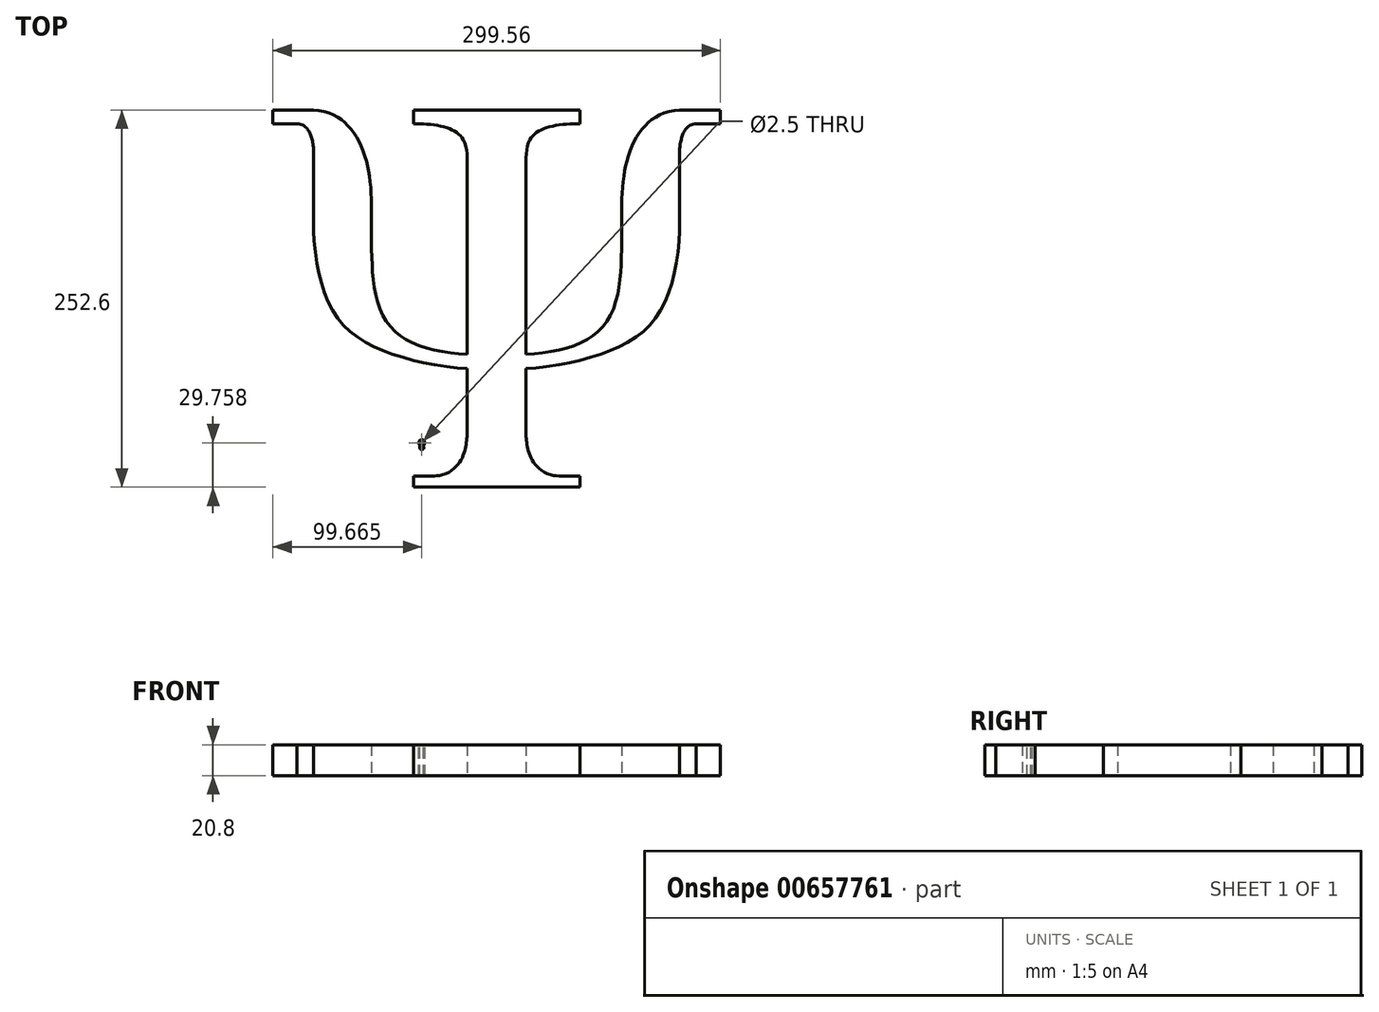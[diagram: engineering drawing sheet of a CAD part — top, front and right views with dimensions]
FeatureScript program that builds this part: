
annotation { "Feature Type Name" : "Feature", "Feature Type Description" : "" }
export const myFeature = defineFeature(function(context is Context, id is Id, definition is map)
    precondition{}
    {
        {
            var Q0;
            Q0=qCreatedBy(makeId("Top.planeOp"),FACE);
            var sketch = newSketch(context, id + "F0", { "sketchPlane" : qUnion([Q0])});
            skLineSegment(sketch, "E0", {"start": v(31.77, -358.04) * mm, "end": v(165.62, -358.04) * mm});
            skLineSegment(sketch, "E1", {"start": v(165.62, -358.04) * mm, "end": v(165.62, -340.15) * mm});
            skLineSegment(sketch, "E2", {"start": v(165.62, -340.15) * mm, "end": v(136.3, -340.15) * mm});
            skLineSegment(sketch, "E3", {"start": v(79.25, 172.15) * mm, "end": v(79.25, -144.4) * mm});
            skFitSpline(sketch, "E4", {"points": [v(136.3, -340.15) * mm, v(128.38, -339.91) * mm, v(119.4, -338.15) * mm, v(107.57, -333.31) * mm, v(99.35, -327.3) * mm, v(93.45, -321.03) * mm, v(88.64, -313.83) * mm, v(85.88, -307.88) * mm, v(83.44, -301.15) * mm, v(82.12, -296.14) * mm, v(81.06, -290.81) * mm, v(80.33, -285.89) * mm, v(79.76, -281.1) * mm, v(79.25, -276.66) * mm], "startDerivative": vector(-97.78, -0.06) * mm, "endDerivative": vector(-8.44, 72.43) * mm});
            skLineSegment(sketch, "E5", {"start": v(165.7, 249.18) * mm, "end": v(165.7, 226.82) * mm});
            skFitSpline(sketch, "E6", {"points": [v(79.25, 172.15) * mm, v(79.89, 182.32) * mm, v(81.67, 191.96) * mm, v(84.08, 198.42) * mm, v(86.92, 203.63) * mm, v(89.38, 206.86) * mm, v(92.37, 209.75) * mm, v(95.31, 212.3) * mm, v(98.88, 214.76) * mm, v(103.12, 216.98) * mm, v(108.23, 219.15) * mm, v(113.63, 221.08) * mm, v(120.47, 222.86) * mm, v(127.56, 224.26) * mm, v(134.93, 225.46) * mm, v(142.7, 226.19) * mm, v(151.51, 226.62) * mm, v(158.7, 226.91) * mm, v(165.7, 226.82) * mm], "startDerivative": vector(5.49, 144.56) * mm, "endDerivative": vector(121.24, -3.12) * mm});
            skLineSegment(sketch, "E7", {"start": v(165.7, 249.18) * mm, "end": v(31.77, 249.18) * mm});
            skLineSegment(sketch, "E8", {"start": v(31.77, -386.97) * mm, "end": v(31.77, 277.63) * mm, "construction": true});
            skLineSegment(sketch, "E9", {"start": v(326.17, 249.18) * mm, "end": v(391.81, 249.18) * mm});
            skLineSegment(sketch, "E10", {"start": v(391.81, 249.18) * mm, "end": v(391.81, 227) * mm});
            skLineSegment(sketch, "E11", {"start": v(391.81, 227) * mm, "end": v(353.15, 227) * mm});
            skLineSegment(sketch, "E12", {"start": v(326.45, 184.52) * mm, "end": v(326.45, 54.15) * mm});
            skFitSpline(sketch, "E13", {"points": [v(353.15, 227) * mm, v(347.86, 226.4) * mm, v(343.18, 224.43) * mm, v(340.35, 222.4) * mm, v(337.49, 219.62) * mm, v(335.67, 217.4) * mm, v(333.64, 214.22) * mm, v(332.38, 211.73) * mm, v(331.02, 208.8) * mm, v(329.92, 205.3) * mm, v(328.99, 201.76) * mm, v(327.86, 197.16) * mm, v(327.11, 192.33) * mm, v(326.69, 188.16) * mm, v(326.45, 184.52) * mm], "startDerivative": vector(-63.94, -2.57) * mm, "endDerivative": vector(-2.98, -52.09) * mm});
            skFitSpline(sketch, "E14", {"points": [v(326.17, 249.18) * mm, v(316, 248.26) * mm, v(305, 245.56) * mm, v(296.12, 241.89) * mm, v(288.72, 237.96) * mm, v(281.77, 233.59) * mm, v(276.3, 228.9) * mm, v(271.02, 223.94) * mm, v(265.5, 217.63) * mm, v(260.02, 210.1) * mm, v(255.2, 202.32) * mm, v(250.76, 193.44) * mm, v(247.02, 184.43) * mm, v(242.9, 172.14) * mm, v(240.33, 162.75) * mm, v(238.4, 154.13) * mm, v(236.73, 143.25) * mm, v(235.12, 131.28) * mm, v(234.1, 118.93) * mm, v(233.51, 106.51) * mm], "startDerivative": vector(-186.8, -10.7) * mm, "endDerivative": vector(-8.46, -209.83) * mm});
            skLineSegment(sketch, "E15", {"start": v(233.51, 106.51) * mm, "end": v(233.51, 37.24) * mm});
            skFitSpline(sketch, "E16", {"points": [v(79.25, -144.4) * mm, v(93.83, -142.98) * mm, v(108.02, -141.34) * mm, v(122.86, -139.02) * mm, v(135.32, -136.34) * mm, v(147.24, -133.02) * mm, v(159.84, -128.88) * mm, v(170.8, -123.92) * mm, v(178.64, -119.69) * mm, v(186.05, -115) * mm, v(193.65, -109) * mm, v(201.2, -101.53) * mm, v(207.12, -94.43) * mm, v(212.26, -86.43) * mm, v(216.85, -77.83) * mm, v(221.08, -67.14) * mm, v(224.4, -56.35) * mm, v(227.36, -44.07) * mm, v(228.9, -34.6) * mm, v(230.46, -22.64) * mm, v(231.68, -9.81) * mm, v(232.14, -1.3) * mm, v(232.64, 12.9) * mm, v(233.05, 25.22) * mm, v(233.51, 37.24) * mm], "startDerivative": vector(312.08, 29.36) * mm, "endDerivative": vector(11.34, 284.18) * mm});
            skFitSpline(sketch, "E17", {"points": [v(79.25, -167.26) * mm, v(90.27, -166.71) * mm, v(103.5, -165.08) * mm, v(117.06, -163.1) * mm, v(136.83, -159.9) * mm, v(149.44, -157.51) * mm, v(161.78, -154.79) * mm, v(177.32, -150.63) * mm, v(188.64, -147.42) * mm, v(201.86, -143) * mm, v(212.97, -138.7) * mm, v(224.08, -134.13) * mm, v(233.63, -129.63) * mm, v(242.7, -124.8) * mm, v(253.33, -118.25) * mm, v(262.33, -111.98) * mm, v(268.67, -106.86) * mm, v(275.69, -100.32) * mm, v(282.57, -92.75) * mm, v(287.89, -85.8) * mm, v(294.16, -75.91) * mm, v(300.1, -65.08) * mm, v(304.93, -54.65) * mm, v(308.27, -46.12) * mm, v(312.22, -34.33) * mm, v(315.16, -23.7) * mm, v(318.7, -9.65) * mm, v(320.75, 0.91) * mm, v(322.86, 14.95) * mm, v(324.9, 31.25) * mm, v(325.59, 42.29) * mm, v(326.45, 54.15) * mm], "startDerivative": vector(347.25, 10.12) * mm, "endDerivative": vector(30.32, 379) * mm});
            skLineSegment(sketch, "E18.trimOffspring", {"start": v(79.25, -167.26) * mm, "end": v(79.25, -276.66) * mm});
            skLineSegment(sketch, "E19", {"start": v(31.77, 249.18) * mm, "end": v(31.77, -358.04) * mm});
            skSolve(sketch);
        }
        {
            var Q0;
            Q0 = qSketchRegion(id + "F0", true);
            extrude(context, id + "F1", {"entities" : qUnion([Q0]), "depth" : 50 * mm, "offsetDistance" : 25 * mm});
        }
        {
            var Q0;
            Q0=makeQuery(id+"F1.opExtrude","SWEPT_BODY",BODY,{"disambiguationData":[OSD([sQuery(id+"F0.wireOp",EDGE,"E0"),sQuery(id+"F0.wireOp",EDGE,"E1"),sQuery(id+"F0.wireOp",EDGE,"E2"),sQuery(id+"F0.wireOp",EDGE,"E3"),sQuery(id+"F0.wireOp",EDGE,"E4"),sQuery(id+"F0.wireOp",EDGE,"E5"),sQuery(id+"F0.wireOp",EDGE,"E6"),sQuery(id+"F0.wireOp",EDGE,"E7"),sQuery(id+"F0.wireOp",EDGE,"E9"),sQuery(id+"F0.wireOp",EDGE,"E10"),sQuery(id+"F0.wireOp",EDGE,"E11"),sQuery(id+"F0.wireOp",EDGE,"E12"),sQuery(id+"F0.wireOp",EDGE,"E13"),sQuery(id+"F0.wireOp",EDGE,"E14"),sQuery(id+"F0.wireOp",EDGE,"E15"),sQuery(id+"F0.wireOp",EDGE,"E16"),sQuery(id+"F0.wireOp",EDGE,"E17"),sQuery(id+"F0.wireOp",EDGE,"E18.trimOffspring"),sQuery(id+"F0.wireOp",EDGE,"E19")])]});
            var Q1;
            Q1=makeQuery(id+"F1.opExtrude","SWEPT_FACE",FACE,{"disambiguationData":[OSD([sQuery(id+"F0.wireOp",EDGE,"E19")])]});
            mirror(context, id + "F2", {"operationType" : NewBodyOperationType.ADD, "entities" : qUnion([Q0]), "mirrorPlane" : qUnion([Q1])});
        }
        {
            var Q0;
            Q0=makeQuery(id+"F1.opExtrude","SWEPT_BODY",BODY,{"disambiguationData":[OSD([sQuery(id+"F0.wireOp",EDGE,"E0"),sQuery(id+"F0.wireOp",EDGE,"E1"),sQuery(id+"F0.wireOp",EDGE,"E2"),sQuery(id+"F0.wireOp",EDGE,"E3"),sQuery(id+"F0.wireOp",EDGE,"E4"),sQuery(id+"F0.wireOp",EDGE,"E5"),sQuery(id+"F0.wireOp",EDGE,"E6"),sQuery(id+"F0.wireOp",EDGE,"E7"),sQuery(id+"F0.wireOp",EDGE,"E9"),sQuery(id+"F0.wireOp",EDGE,"E10"),sQuery(id+"F0.wireOp",EDGE,"E11"),sQuery(id+"F0.wireOp",EDGE,"E12"),sQuery(id+"F0.wireOp",EDGE,"E13"),sQuery(id+"F0.wireOp",EDGE,"E14"),sQuery(id+"F0.wireOp",EDGE,"E15"),sQuery(id+"F0.wireOp",EDGE,"E16"),sQuery(id+"F0.wireOp",EDGE,"E17"),sQuery(id+"F0.wireOp",EDGE,"E18.trimOffspring"),sQuery(id+"F0.wireOp",EDGE,"E19")])]});
            var Q1;
            Q1=makeQuery(id+"F2.opPattern","COPY",VERTEX,{"derivedFrom":makeQuery(id+"F1.opExtrude","CAP_VERTEX",VERTEX,{"disambiguationData":[OSD([sQuery(id+"F0.wireOp",EDGE,"E0"),sQuery(id+"F0.wireOp",EDGE,"E1")])],"isStart":false}),"instanceName":"1"});
            transform(context, id + "F3", {"entities" : qUnion([Q0]), "transformType" : TransformType.SCALE_UNIFORMLY, "scale" : .416, "scalePoint" : qUnion([Q1]), "makeCopy" : false});
        }
        {
            var Q0;
            {var subQ0=makeQuery(id+"F1.opExtrude","CAP_FACE",FACE,{"disambiguationData":[OSD([sQuery(id+"F0.wireOp",EDGE,"E0"),sQuery(id+"F0.wireOp",EDGE,"E1"),sQuery(id+"F0.wireOp",EDGE,"E2"),sQuery(id+"F0.wireOp",EDGE,"E3"),sQuery(id+"F0.wireOp",EDGE,"E4"),sQuery(id+"F0.wireOp",EDGE,"E5"),sQuery(id+"F0.wireOp",EDGE,"E6"),sQuery(id+"F0.wireOp",EDGE,"E7"),sQuery(id+"F0.wireOp",EDGE,"E9"),sQuery(id+"F0.wireOp",EDGE,"E10"),sQuery(id+"F0.wireOp",EDGE,"E11"),sQuery(id+"F0.wireOp",EDGE,"E12"),sQuery(id+"F0.wireOp",EDGE,"E13"),sQuery(id+"F0.wireOp",EDGE,"E14"),sQuery(id+"F0.wireOp",EDGE,"E15"),sQuery(id+"F0.wireOp",EDGE,"E16"),sQuery(id+"F0.wireOp",EDGE,"E17"),sQuery(id+"F0.wireOp",EDGE,"E18.trimOffspring"),sQuery(id+"F0.wireOp",EDGE,"E19")])],"isStart":false});Q0=makeQuery(id+"F2.boolean.opBoolean","MERGE",FACE,{"derivedFrom":[subQ0,makeQuery(id+"F2.opPattern","COPY",FACE,{"derivedFrom":subQ0,"instanceName":"1"})]});}
            var sketch = newSketch(context, id + "F4", { "sketchPlane" : qUnion([Q0])});
            skCircle(sketch, "E20", {"center": v(-96.51, -328.28) * mm, "radius": 1.25 * mm});
            skLineSegment(sketch, "E21", {"start": v(-96.51, -332.78) * mm, "end": v(-96.51, -328.28) * mm, "construction": true});
            skArc(sketch, "E22", {"start": v(-94.83, -329.35) * mm, "mid": v(-96.51, -326.28) * mm, "end": v(-98.2, -329.35) * mm});
            skLineSegment(sketch, "E23", {"start": v(-98.51, -332.78) * mm, "end": v(-94.51, -332.78) * mm});
            skArc(sketch, "E24", {"start": v(-98.51, -332.78) * mm, "mid": v(-97.78, -331.12) * mm, "end": v(-98.2, -329.35) * mm});
            skArc(sketch, "E25", {"start": v(-94.83, -329.35) * mm, "mid": v(-95.25, -331.12) * mm, "end": v(-94.51, -332.78) * mm});
            skSolve(sketch);
        }
        {
            var Q0;
            Q0 = qSketchRegion(id + "F4", true);
            var Q1;
            {var subQ0=makeQuery(id+"F1.opExtrude","CAP_FACE",FACE,{"disambiguationData":[OSD([sQuery(id+"F0.wireOp",EDGE,"E0"),sQuery(id+"F0.wireOp",EDGE,"E1"),sQuery(id+"F0.wireOp",EDGE,"E2"),sQuery(id+"F0.wireOp",EDGE,"E3"),sQuery(id+"F0.wireOp",EDGE,"E4"),sQuery(id+"F0.wireOp",EDGE,"E5"),sQuery(id+"F0.wireOp",EDGE,"E6"),sQuery(id+"F0.wireOp",EDGE,"E7"),sQuery(id+"F0.wireOp",EDGE,"E9"),sQuery(id+"F0.wireOp",EDGE,"E10"),sQuery(id+"F0.wireOp",EDGE,"E11"),sQuery(id+"F0.wireOp",EDGE,"E12"),sQuery(id+"F0.wireOp",EDGE,"E13"),sQuery(id+"F0.wireOp",EDGE,"E14"),sQuery(id+"F0.wireOp",EDGE,"E15"),sQuery(id+"F0.wireOp",EDGE,"E16"),sQuery(id+"F0.wireOp",EDGE,"E17"),sQuery(id+"F0.wireOp",EDGE,"E18.trimOffspring"),sQuery(id+"F0.wireOp",EDGE,"E19")])],"isStart":true});Q1=makeQuery(id+"F2.boolean.opBoolean","MERGE",FACE,{"derivedFrom":[subQ0,makeQuery(id+"F2.opPattern","COPY",FACE,{"derivedFrom":subQ0,"instanceName":"1"})]});}
            extrude(context, id + "F5", {"entities" : qUnion([Q0]), "operationType" : NewBodyOperationType.ADD, "endBound" : BoundingType.UP_TO_SURFACE, "oppositeDirection" : true, "depth" : 25 * mm, "endBoundEntityFace" : qUnion([Q1]), "offsetDistance" : 25 * mm});
        }
        {
            var Q0;
            Q0=makeQuery(id+"F5.opExtrude","SWEPT_EDGE",EDGE,{"disambiguationData":[OSD([sQuery(id+"F0.wireOp",EDGE,"E7"),sQuery(id+"F4.wireOp",EDGE,"cKUMz4s3-V6vC-xERQ-K8Lx-FbgcmSv3Mrfl"),sQuery(id+"F4.wireOp",EDGE,"E23")])]});
            var Q1;
            Q1=makeQuery(id+"F5.opExtrude","SWEPT_EDGE",EDGE,{"disambiguationData":[OSD([sQuery(id+"F0.wireOp",EDGE,"E7"),sQuery(id+"F4.wireOp",EDGE,"KZUPpUWQ-8Gm4-iEDg-FZ3v-jHX8nOhChIJV"),sQuery(id+"F4.wireOp",EDGE,"E23")])]});
            fillet(context, id + "F6", {"entities" : qUnion([Q0, Q1]), "radius" : 1 * mm, "tangentPropagation" : true, "allowEdgeOverflow" : false});
        }
    });
